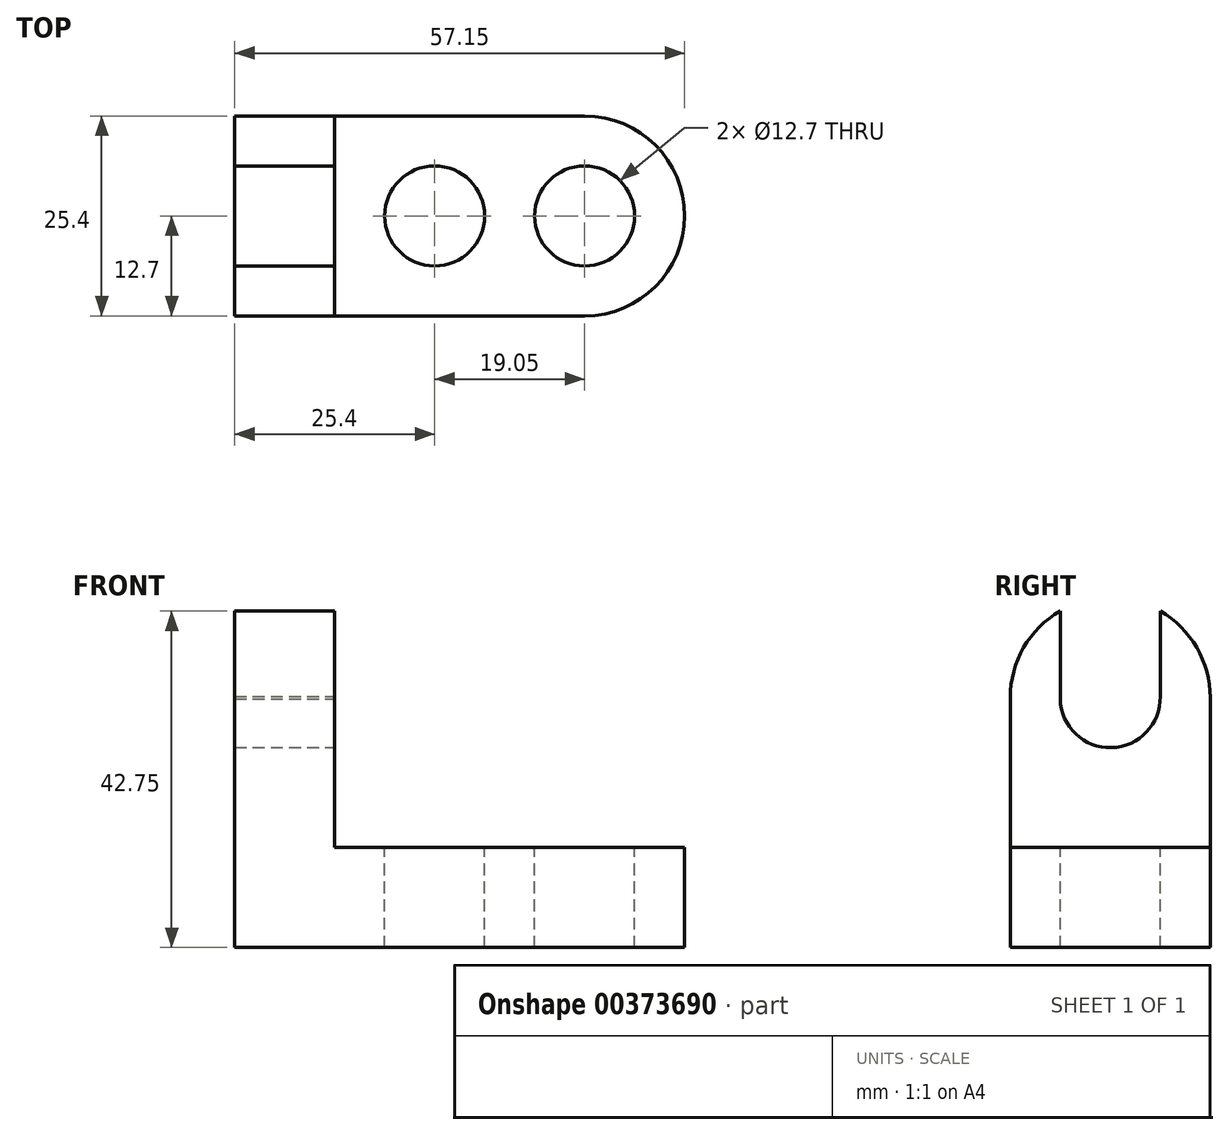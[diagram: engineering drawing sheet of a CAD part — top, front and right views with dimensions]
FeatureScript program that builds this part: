
annotation { "Feature Type Name" : "Feature", "Feature Type Description" : "" }
export const myFeature = defineFeature(function(context is Context, id is Id, definition is map)
    precondition{}
    {
        {
            var Q0;
            Q0=qCreatedBy(makeId("Front.planeOp"),FACE);
            var sketch = newSketch(context, id + "F0", { "sketchPlane" : qUnion([Q0])});
            skLineSegment(sketch, "E0", {"start": v(0, 0) * mm, "end": v(0, 44.45) * mm});
            skLineSegment(sketch, "E1", {"start": v(0, 44.45) * mm, "end": v(12.7, 44.45) * mm});
            skLineSegment(sketch, "E2", {"start": v(12.7, 44.45) * mm, "end": v(12.7, 12.7) * mm});
            skLineSegment(sketch, "E3", {"start": v(12.7, 12.7) * mm, "end": v(57.15, 12.7) * mm});
            skLineSegment(sketch, "E4", {"start": v(57.15, 12.7) * mm, "end": v(57.15, 0) * mm});
            skLineSegment(sketch, "E5", {"start": v(57.15, 0) * mm, "end": v(0, 0) * mm});
            skSolve(sketch);
        }
        {
            var Q0;
            Q0=makeQuery(id+"F0.imprint","IMPRINT",FACE,{"disambiguationData":[TD([[makeQuery(id+"F0.imprint","IMPRINT",EDGE,{"derivedFrom":sQuery(id+"F0.wireOp",EDGE,"E0")}),-1.0]])]});
            extrude(context, id + "F1", {"entities" : qUnion([Q0]), "depth" : 25.4 * mm});
        }
        {
            var Q0;
            Q0=makeQuery(id+"F1.opExtrude","SWEPT_FACE",FACE,{"disambiguationData":[OSD([sQuery(id+"F0.wireOp",EDGE,"E2")])]});
            var sketch = newSketch(context, id + "F2", { "sketchPlane" : qUnion([Q0])});
            skCircle(sketch, "E6", {"center": v(-12.7, 31.75) * mm, "radius": 6.35 * mm});
            skPoint(sketch, "E6.centerSnap0", {"position": v(-12.7, 44.45) * mm});
            skArc(sketch, "E7", {"start": v(0, 31.75) * mm, "mid": v(-12.7, 44.45) * mm, "end": v(-25.4, 31.75) * mm});
            skLineSegment(sketch, "E8", {"start": v(-19.05, 31.59) * mm, "end": v(-19.05, 44.45) * mm});
            skLineSegment(sketch, "E9", {"start": v(-6.35, 31.91) * mm, "end": v(-6.35, 44.45) * mm});
            skSolve(sketch);
        }
        {
            var Q0;
            {var subQ0=sQuery(id+"F2.wireOp",EDGE,"E7");var subQ1=sQuery(id+"F0.wireOp",EDGE,"E2");var subQ2=makeQuery(id+"F1.opExtrude","CAP_EDGE",EDGE,{"disambiguationData":[OSD([subQ1])],"isStart":false});var subQ3=makeQuery(id+"F2.imprint","INTERSECT",VERTEX,{"derivedFrom":[subQ2,subQ0]});Q0=makeQuery(id+"F2.imprint","IMPRINT",FACE,{"disambiguationData":[TD([[makeQuery(id+"F2.imprint","IMPRINT",EDGE,{"disambiguationData":[TD([[subQ3,1.0]])],"derivedFrom":subQ0}),-1.0]])]});}
            var Q1;
            {var subQ0=sQuery(id+"F2.wireOp",EDGE,"E8");var subQ1=sQuery(id+"F2.wireOp",EDGE,"E7");var subQ2=makeQuery(id+"F2.imprint","INTERSECT",VERTEX,{"derivedFrom":[subQ1,subQ0]});Q1=makeQuery(id+"F2.imprint","IMPRINT",FACE,{"disambiguationData":[TD([[makeQuery(id+"F2.imprint","IMPRINT",EDGE,{"disambiguationData":[TD([[subQ2,1.0]])],"derivedFrom":subQ1}),-1.0]])]});}
            var Q2;
            {var subQ0=sQuery(id+"F2.wireOp",EDGE,"E9");var subQ1=sQuery(id+"F2.wireOp",EDGE,"E7");var subQ2=makeQuery(id+"F2.imprint","INTERSECT",VERTEX,{"derivedFrom":[subQ1,subQ0]});Q2=makeQuery(id+"F2.imprint","IMPRINT",FACE,{"disambiguationData":[TD([[makeQuery(id+"F2.imprint","IMPRINT",EDGE,{"disambiguationData":[TD([[subQ2,-1.0]])],"derivedFrom":subQ1}),-1.0]])]});}
            var Q3;
            {var subQ0=sQuery(id+"F2.wireOp",EDGE,"E7");var subQ1=sQuery(id+"F0.wireOp",EDGE,"E2");var subQ2=makeQuery(id+"F1.opExtrude","CAP_EDGE",EDGE,{"disambiguationData":[OSD([subQ1])],"isStart":true});var subQ3=makeQuery(id+"F2.imprint","INTERSECT",VERTEX,{"derivedFrom":[subQ2,subQ0]});Q3=makeQuery(id+"F2.imprint","IMPRINT",FACE,{"disambiguationData":[TD([[makeQuery(id+"F2.imprint","IMPRINT",EDGE,{"disambiguationData":[TD([[subQ3,-1.0]])],"derivedFrom":subQ0}),-1.0]])]});}
            var Q4;
            {var subQ0=sQuery(id+"F2.wireOp",EDGE,"E6");var subQ1=makeQuery(id+"F2.imprint","INTERSECT",VERTEX,{"derivedFrom":[subQ0,sQuery(id+"F2.wireOp",EDGE,"E9")]});Q4=makeQuery(id+"F2.imprint","IMPRINT",FACE,{"disambiguationData":[TD([[makeQuery(id+"F2.imprint","IMPRINT",EDGE,{"disambiguationData":[TD([[subQ1,-1.0]])],"derivedFrom":subQ0}),1.0]])]});}
            var Q5;
            {var subQ1=sQuery(id+"F2.wireOp",EDGE,"E6");var subQ5=sQuery(id+"F2.wireOp",EDGE,"E9");var subQ8=makeQuery(id+"F2.imprint","INTERSECT",VERTEX,{"derivedFrom":[subQ1,subQ5]});Q5=makeQuery(id+"F2.imprint","IMPRINT",FACE,{"disambiguationData":[TD([[makeQuery(id+"F2.imprint","IMPRINT",EDGE,{"disambiguationData":[TD([[subQ8,-1.0]])],"derivedFrom":subQ1}),-1.0]])]});}
            extrude(context, id + "F3", {"entities" : qUnion([Q0, Q1, Q2, Q3, Q4, Q5]), "operationType" : NewBodyOperationType.REMOVE, "oppositeDirection" : true, "depth" : 25.4 * mm});
        }
        {
            var Q0;
            Q0=makeQuery(id+"F1.opExtrude","SWEPT_FACE",FACE,{"disambiguationData":[OSD([sQuery(id+"F0.wireOp",EDGE,"E3")])]});
            var sketch = newSketch(context, id + "F4", { "sketchPlane" : qUnion([Q0])});
            skCircle(sketch, "E10", {"center": v(44.45, -12.7) * mm, "radius": 6.35 * mm});
            skPoint(sketch, "E10.centerSnap0", {"position": v(57.15, -12.7) * mm});
            skCircle(sketch, "E11", {"center": v(25.4, -12.7) * mm, "radius": 6.35 * mm});
            skPoint(sketch, "E11.centerSnap0", {"position": v(12.7, -12.7) * mm});
            skLineSegment(sketch, "E12", {"start": v(25.4, -6.35) * mm, "end": v(25.4, -19.05) * mm});
            skLineSegment(sketch, "E13", {"start": v(44.45, -19.05) * mm, "end": v(44.45, -6.35) * mm});
            skArc(sketch, "E14", {"start": v(44.45, -25.4) * mm, "mid": v(57.15, -12.7) * mm, "end": v(44.45, 0) * mm});
            skSolve(sketch);
        }
        {
            var Q0;
            {var subQ0=sQuery(id+"F4.wireOp",EDGE,"E12");Q0=makeQuery(id+"F4.imprint","IMPRINT",FACE,{"disambiguationData":[TD([[makeQuery(id+"F4.imprint","IMPRINT",EDGE,{"derivedFrom":subQ0}),-1.0]])]});}
            var Q1;
            {var subQ0=sQuery(id+"F4.wireOp",EDGE,"E12");Q1=makeQuery(id+"F4.imprint","IMPRINT",FACE,{"disambiguationData":[TD([[makeQuery(id+"F4.imprint","IMPRINT",EDGE,{"derivedFrom":subQ0}),1.0]])]});}
            var Q2;
            {var subQ0=sQuery(id+"F4.wireOp",EDGE,"E13");Q2=makeQuery(id+"F4.imprint","IMPRINT",FACE,{"disambiguationData":[TD([[makeQuery(id+"F4.imprint","IMPRINT",EDGE,{"derivedFrom":subQ0}),1.0]])]});}
            var Q3;
            {var subQ0=sQuery(id+"F4.wireOp",EDGE,"E13");Q3=makeQuery(id+"F4.imprint","IMPRINT",FACE,{"disambiguationData":[TD([[makeQuery(id+"F4.imprint","IMPRINT",EDGE,{"derivedFrom":subQ0}),-1.0]])]});}
            var Q4;
            {var subQ0=sQuery(id+"F4.wireOp",EDGE,"E14");var subQ1=sQuery(id+"F0.wireOp",EDGE,"E3");var subQ2=makeQuery(id+"F1.opExtrude","CAP_EDGE",EDGE,{"disambiguationData":[OSD([subQ1])],"isStart":true});var subQ3=makeQuery(id+"F4.imprint","INTERSECT",VERTEX,{"derivedFrom":[subQ2,subQ0]});Q4=makeQuery(id+"F4.imprint","IMPRINT",FACE,{"disambiguationData":[TD([[makeQuery(id+"F4.imprint","IMPRINT",EDGE,{"disambiguationData":[TD([[subQ3,1.0]])],"derivedFrom":subQ0}),-1.0]])]});}
            var Q5;
            {var subQ0=sQuery(id+"F4.wireOp",EDGE,"E14");var subQ1=sQuery(id+"F0.wireOp",EDGE,"E3");var subQ2=makeQuery(id+"F1.opExtrude","CAP_EDGE",EDGE,{"disambiguationData":[OSD([subQ1])],"isStart":false});var subQ3=makeQuery(id+"F4.imprint","INTERSECT",VERTEX,{"derivedFrom":[subQ2,subQ0]});Q5=makeQuery(id+"F4.imprint","IMPRINT",FACE,{"disambiguationData":[TD([[makeQuery(id+"F4.imprint","IMPRINT",EDGE,{"disambiguationData":[TD([[subQ3,-1.0]])],"derivedFrom":subQ0}),-1.0]])]});}
            extrude(context, id + "F5", {"entities" : qUnion([Q0, Q1, Q2, Q3, Q4, Q5]), "operationType" : NewBodyOperationType.REMOVE, "oppositeDirection" : true, "depth" : 25.4 * mm});
        }
    });
